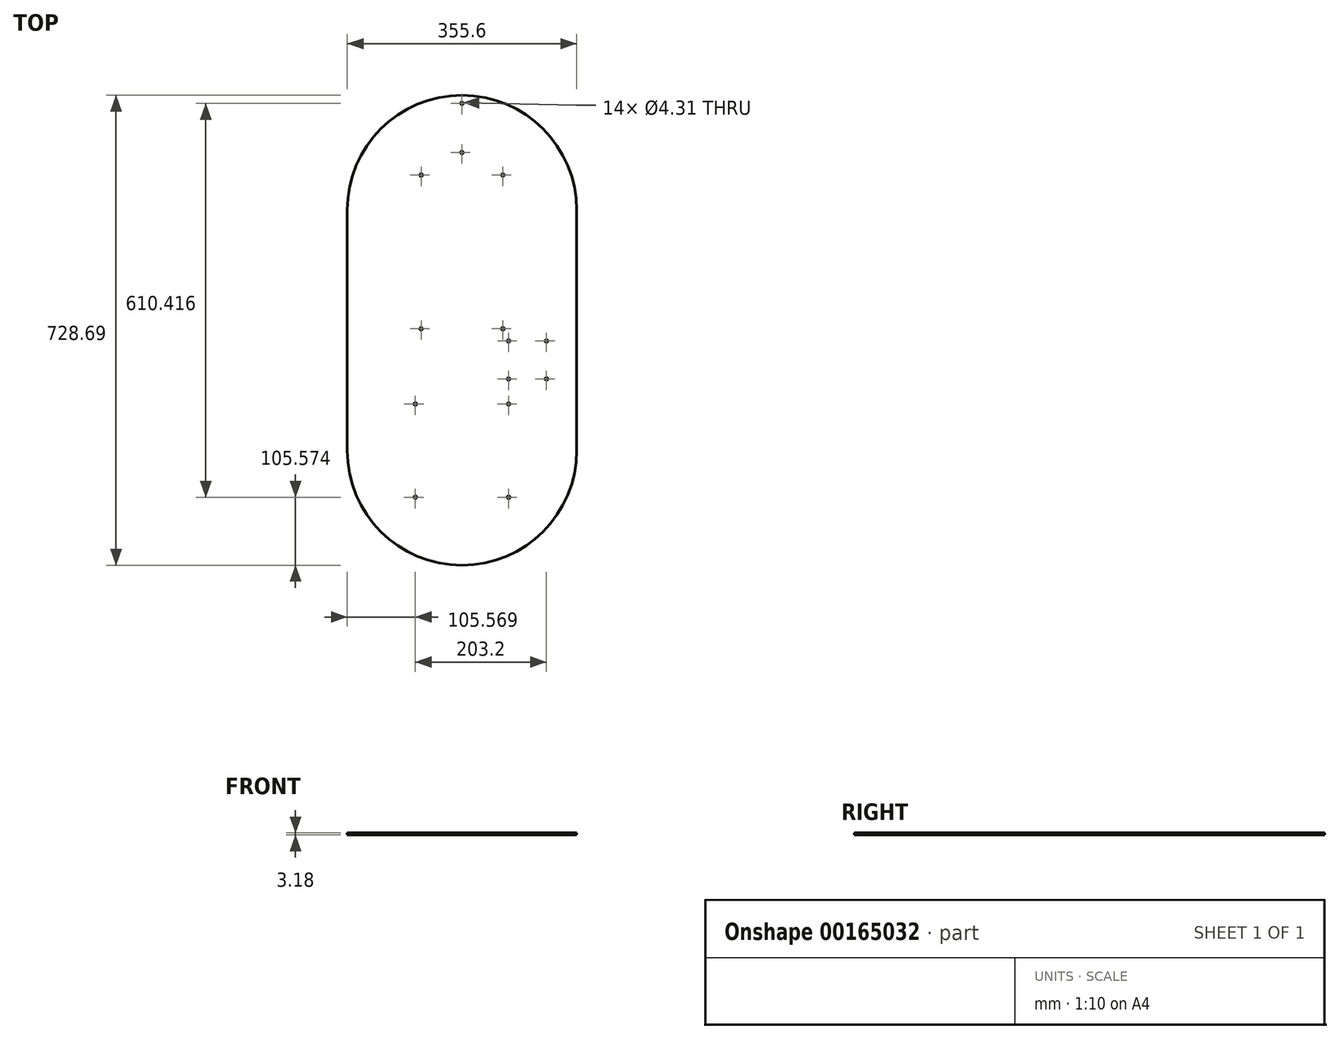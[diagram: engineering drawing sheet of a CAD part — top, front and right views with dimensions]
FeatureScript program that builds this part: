
annotation { "Feature Type Name" : "Feature", "Feature Type Description" : "" }
export const myFeature = defineFeature(function(context is Context, id is Id, definition is map)
    precondition{}
    {
        {
            var Q0;
            Q0=qCreatedBy(makeId("Top.planeOp"),FACE);
            var sketch = newSketch(context, id + "F0", { "sketchPlane" : qUnion([Q0])});
            skLineSegment(sketch, "E0.top", {"start": v(0, -373.09) * mm, "end": v(355.6, -373.09) * mm, "construction": true});
            skLineSegment(sketch, "E0.left", {"start": v(0, 0) * mm, "end": v(0, -373.09) * mm});
            skLineSegment(sketch, "E0.right", {"start": v(355.6, 0) * mm, "end": v(355.6, -373.09) * mm});
            skArc(sketch, "E1", {"start": v(0, -373.09) * mm, "mid": v(177.8, -550.89) * mm, "end": v(355.6, -373.09) * mm});
            skLineSegment(sketch, "E2", {"start": v(177.8, -65.09) * mm, "end": v(177.8, -184.26) * mm, "construction": true});
            skLineSegment(sketch, "E3", {"start": v(177.8, -65.09) * mm, "end": v(177.8, 54.08) * mm, "construction": true});
            skLineSegment(sketch, "E4", {"start": v(114.5, 54.08) * mm, "end": v(241.1, 54.08) * mm, "construction": true});
            skLineSegment(sketch, "E5", {"start": v(241.1, 54.08) * mm, "end": v(177.8, -65.09) * mm, "construction": true});
            skLineSegment(sketch, "E6", {"start": v(177.8, -65.09) * mm, "end": v(114.5, 54.08) * mm, "construction": true});
            skLineSegment(sketch, "E7", {"start": v(114.5, -184.26) * mm, "end": v(241.1, -184.26) * mm, "construction": true});
            skLineSegment(sketch, "E8", {"start": v(177.8, -184.26) * mm, "end": v(177.8, -232.57) * mm, "construction": true});
            skLineSegment(sketch, "E9", {"start": v(177.8, -232.57) * mm, "end": v(279.4, -232.57) * mm, "construction": true});
            skLineSegment(sketch, "E10.bottom", {"start": v(308.77, -203.2) * mm, "end": v(250.03, -203.2) * mm, "construction": true});
            skLineSegment(sketch, "E10.top", {"start": v(308.77, -261.94) * mm, "end": v(250.03, -261.94) * mm, "construction": true});
            skLineSegment(sketch, "E10.left", {"start": v(308.77, -203.2) * mm, "end": v(308.77, -261.94) * mm, "construction": true});
            skLineSegment(sketch, "E10.right", {"start": v(250.03, -203.2) * mm, "end": v(250.03, -261.94) * mm, "construction": true});
            skPoint(sketch, "E10.middle", {"position": v(279.4, -232.57) * mm});
            skLineSegment(sketch, "E11.bottom", {"start": v(250.03, -300.85) * mm, "end": v(105.57, -300.85) * mm, "construction": true});
            skLineSegment(sketch, "E11.top", {"start": v(250.03, -445.32) * mm, "end": v(105.57, -445.32) * mm, "construction": true});
            skLineSegment(sketch, "E11.left", {"start": v(250.03, -300.85) * mm, "end": v(250.03, -445.32) * mm, "construction": true});
            skLineSegment(sketch, "E11.right", {"start": v(105.57, -300.85) * mm, "end": v(105.57, -445.32) * mm, "construction": true});
            skCircle(sketch, "E12", {"center": v(105.57, -300.85) * mm, "radius": 2.15 * mm});
            skCircle(sketch, "E13", {"center": v(250.03, -300.85) * mm, "radius": 2.15 * mm});
            skCircle(sketch, "E14", {"center": v(105.57, -445.32) * mm, "radius": 2.15 * mm});
            skCircle(sketch, "E15", {"center": v(250.03, -445.32) * mm, "radius": 2.15 * mm});
            skCircle(sketch, "E16", {"center": v(250.03, -203.2) * mm, "radius": 2.15 * mm});
            skCircle(sketch, "E17", {"center": v(250.03, -261.94) * mm, "radius": 2.15 * mm});
            skCircle(sketch, "E18", {"center": v(308.77, -261.94) * mm, "radius": 2.15 * mm});
            skCircle(sketch, "E19", {"center": v(308.77, -203.2) * mm, "radius": 2.15 * mm});
            skCircle(sketch, "E20", {"center": v(114.5, -184.26) * mm, "radius": 2.15 * mm});
            skCircle(sketch, "E21", {"center": v(241.1, -184.26) * mm, "radius": 2.15 * mm});
            skCircle(sketch, "E22", {"center": v(241.1, 54.08) * mm, "radius": 2.15 * mm});
            skCircle(sketch, "E23", {"center": v(114.5, 54.08) * mm, "radius": 2.15 * mm});
            skLineSegment(sketch, "E24", {"start": v(0, 0) * mm, "end": v(118.53, 0) * mm, "construction": true});
            skLineSegment(sketch, "E25", {"start": v(118.53, 0) * mm, "end": v(118.53, -65.09) * mm, "construction": true});
            skLineSegment(sketch, "E26", {"start": v(118.53, -65.09) * mm, "end": v(237.07, -65.09) * mm, "construction": true});
            skLineSegment(sketch, "E27", {"start": v(237.07, -65.09) * mm, "end": v(237.07, 0) * mm, "construction": true});
            skLineSegment(sketch, "E28", {"start": v(237.07, 0) * mm, "end": v(355.6, 0) * mm, "construction": true});
            skArc(sketch, "E29", {"start": v(355.6, 0) * mm, "mid": v(177.8, 177.8) * mm, "end": v(0, 0) * mm});
            skLineSegment(sketch, "E30", {"start": v(177.8, 177.8) * mm, "end": v(177.8, 165.1) * mm, "construction": true});
            skLineSegment(sketch, "E31", {"start": v(177.8, 165.1) * mm, "end": v(177.8, 88.9) * mm, "construction": true});
            skCircle(sketch, "E32", {"center": v(177.8, 165.1) * mm, "radius": 2.15 * mm});
            skCircle(sketch, "E33", {"center": v(177.8, 88.9) * mm, "radius": 2.15 * mm});
            skArc(sketch, "E34", {"start": v(241.1, 54.08) * mm, "mid": v(177.8, 69.85) * mm, "end": v(114.5, 54.08) * mm, "construction": true});
            skLineSegment(sketch, "E35", {"start": v(177.8, 88.9) * mm, "end": v(177.8, 69.85) * mm, "construction": true});
            skCircle(sketch, "E36", {"center": v(177.8, -373.09) * mm, "radius": 127 * mm, "construction": true});
            skCircle(sketch, "E37", {"center": v(250.03, -261.94) * mm, "radius": 5.56 * mm, "construction": true});
            skSolve(sketch);
        }
        {
            var Q0;
            Q0=qSketchRegion(id+"F0",true);
            extrude(context, id + "F1", {"entities" : qUnion([Q0]), "depth" : 3.17 * mm});
        }
    });
